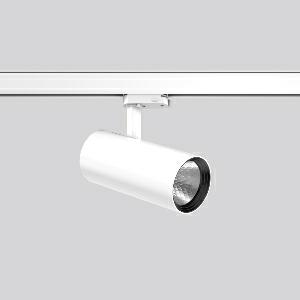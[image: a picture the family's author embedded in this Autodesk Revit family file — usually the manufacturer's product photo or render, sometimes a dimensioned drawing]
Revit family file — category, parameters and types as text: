
# Revit family: deecos_s_mini_742196_002_76_1d7b
name_source: partatom
category: Lighting Fixtures
units: mm (PartAtom-declared; Revit-internal decimal feet)

## family parameters
Cut with Voids When Loaded = No
Host = Face
Light Source = No
Part Type = Normal
Room Calculation Point = No
Round Connector Dimension = Use Diameter
Shared = No

## types (1)
- DEECOS S mini (1 x LED Modul 930, 2450 lm, 3000)
    Apparent Load = 20 VA
    Approval mark = CE
    CIE Flux Codes = 99 100 100 100 100
    Color Rendering = 90
    Color Temperature = 3000
    Default Elevation = 1800 mm
    Description = Series: DEECOS S mini
LED surface-mounted projector in modern design with no visible cooling ribs. Housing: die-cast aluminium, powder-coated. Rotation range: 356°. Swivel range: 90°. Black plastic ring and recessed LED to prevent glare from the side. Optical assembly with reflector made of MIRO-Silver with 98% total light reflection for outstanding efficiency - can be changed without tools. Best colour rendering index Ra>90. With adapter for RZB 3-circuit DALI tracks. Suitable for Track on ceiling, Wall track. High quality converter without flickering and stroboscopic effect. The following accessories can be mounted without use of tools: interchangeable lenses, decorative glasses, honeycomb louvre, clear and frosted diffusers, white interchangeable plastic ring. 
Colour: traffic white, matt (RAL 9016)
Diameter: 87 mm
Height: 214 mm
Lamp: LED
Socket: without socket
Colour temperature: 3000K
Colour rendering index (CRI): 92
System power: 20 W
Rated luminous flux: 2450 lm
Luminous efficiency: 123 lm/W
Control gear: Converter, dimmable, DALI
Protection class: I
Type of protection: IP 20
    Height = 214 mm
    Lamp = 1 x LED Modul 930
    Lamp Light Flux = 2450 lm
    Lamp count = 1
    Length = 87 mm
    Lifetime = 50000 h
    Luminous efficacy = 123 lm/W
    Manufacturer = RZB
    ModVariant = No
    Model = 742196.002.76
    Mounting Place = Ceiling
    Mounting Type = Rail mounted
    Number of Poles = 1
    OnlyDefault = Yes
    Power Factor = 1
    Product Name = DEECOS S mini
    Product group = Track mounted projectors
    ProductGroupID = 301
    Protection Class = Protection class I
    Protection Degree = IP 20
    RLX_Detail_Level = 1
    RLX_Emergency_Light_Flux = 0 lm
    RLX_Emergency_Type = 0
    RLX_Emergency_Type_DB = No
    RlxData = <blob elided: 35361 chars, md5=7692109c>
    Socket = socket
    Standby Power = 0 W
    System Light Flux = 2450 lm
    System Power = 20 W
    Type Comments = Product without accessories
    Type Image = 741926.002.jpg
    URL = http://relux.com
    VarID = ---
    Voltage = 230 V
    Voltage Range = 220-240 V
    Weight = 0.00 kg
    Width = 0 mm  [stored 0 ft]

note: [stored X ft] marks values corroborated as IEEE doubles in the binary element streams (Revit-internal decimal feet)

## geometry (parser evidence)
native form markers: Blend x4, Sweep x13
no freeform markers — native parametric forms only
